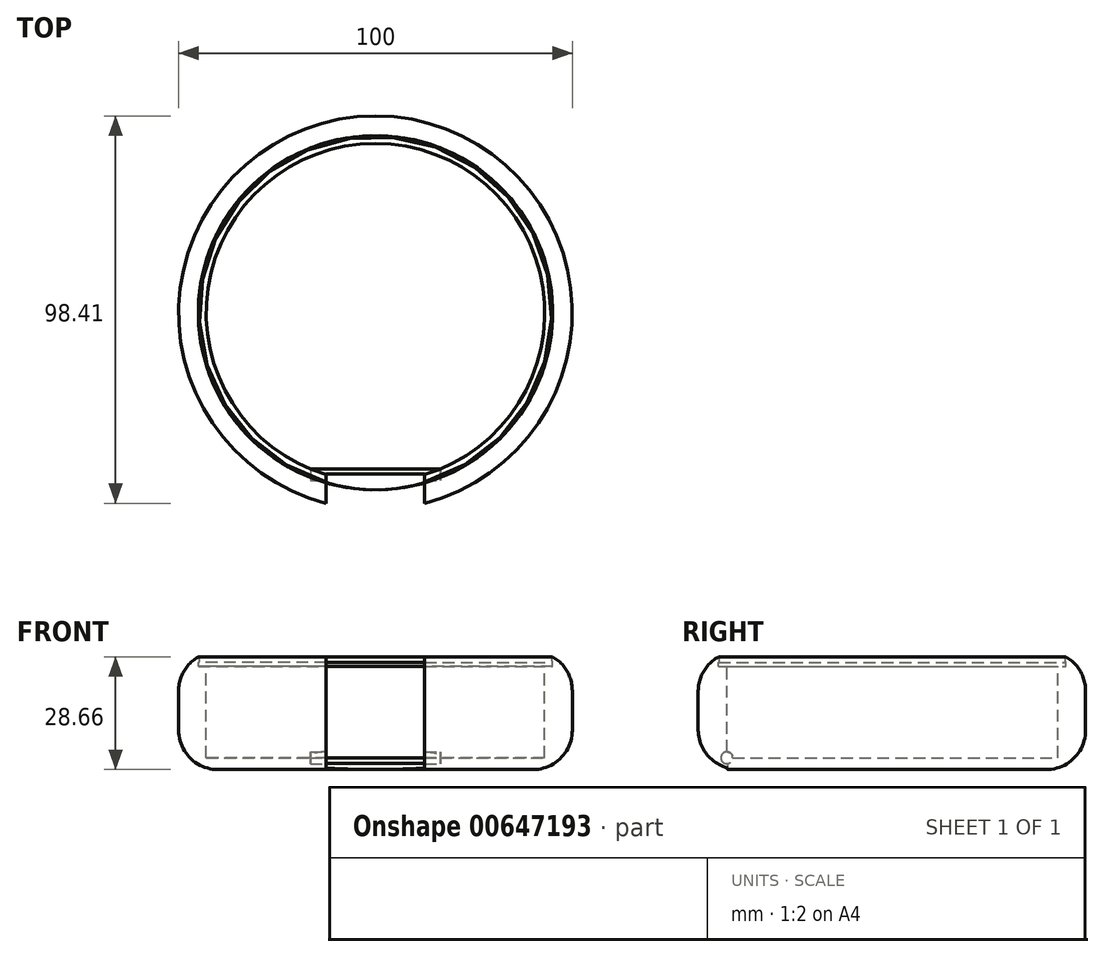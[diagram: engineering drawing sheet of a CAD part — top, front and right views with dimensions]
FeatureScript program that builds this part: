
annotation { "Feature Type Name" : "Feature", "Feature Type Description" : "" }
export const myFeature = defineFeature(function(context is Context, id is Id, definition is map)
    precondition{}
    {
        {
            var Q0;
            Q0=qCreatedBy(makeId("Top.planeOp"),FACE);
            var sketch = newSketch(context, id + "F0", { "sketchPlane" : qUnion([Q0])});
            skCircle(sketch, "E0", {"center": v(0, 0) * mm, "radius": 50 * mm});
            skSolve(sketch);
        }
        {
            var Q0;
            Q0=makeQuery(id+"F0.imprint","IMPRINT",FACE,{"disambiguationData":[TD([[makeQuery(id+"F0.imprint","IMPRINT",EDGE,{"derivedFrom":sQuery(id+"F0.wireOp",EDGE,"E0")}),1.0]])]});
            extrude(context, id + "F1", {"entities" : qUnion([Q0]), "depth" : 30 * mm, "offsetDistance" : 25 * mm});
        }
        {
            var Q0;
            Q0=makeQuery(id+"F1.opExtrude","CAP_FACE",FACE,{"disambiguationData":[OSD([sQuery(id+"F0.wireOp",EDGE,"E0")])],"isStart":false});
            var Q1;
            Q1=makeQuery(id+"F1.opExtrude","CAP_EDGE",EDGE,{"disambiguationData":[OSD([sQuery(id+"F0.wireOp",EDGE,"E0")])],"isStart":true});
            fillet(context, id + "F2", {"entities" : qUnion([Q0, Q1]), "radius" : 10 * mm, "tangentPropagation" : true, "allowEdgeOverflow" : false});
        }
        {
            var Q0;
            Q0=makeQuery(id+"F1.opExtrude","CAP_FACE",FACE,{"disambiguationData":[OSD([sQuery(id+"F0.wireOp",EDGE,"E0")])],"isStart":false});
            var sketch = newSketch(context, id + "F3", { "sketchPlane" : qUnion([Q0])});
            skCircle(sketch, "E1", {"center": v(0, 0) * mm, "radius": 43 * mm});
            skSolve(sketch);
        }
        {
            var Q0;
            Q0 = qSketchRegion(id + "F3", true);
            extrude(context, id + "F4", {"entities" : qUnion([Q0]), "operationType" : NewBodyOperationType.REMOVE, "oppositeDirection" : true, "depth" : 27 * mm, "offsetDistance" : 25 * mm});
        }
        {
            var Q0;
            Q0=qCreatedBy(makeId("Front.planeOp"),FACE);
            cPlane(context, id + "F5", {"entities" : qUnion([Q0]), "cplaneType" : CPlaneType.OFFSET, "offset" : 50 * mm, "width" : 150 * mm, "height" : 150 * mm});
        }
        {
            var Q0;
            Q0=qCreatedBy(id+"F5.planeOp",FACE);
            var sketch = newSketch(context, id + "F6", { "sketchPlane" : qUnion([Q0])});
            skLineSegment(sketch, "E2", {"start": v(0, 0) * mm, "end": v(0, 30) * mm});
            skLineSegment(sketch, "E3", {"start": v(0, 30) * mm, "end": v(12.5, 30) * mm});
            skLineSegment(sketch, "E4", {"start": v(12.5, 30) * mm, "end": v(12.5, 0) * mm});
            skLineSegment(sketch, "E5", {"start": v(12.5, 0) * mm, "end": v(0, 0) * mm});
            skLineSegment(sketch, "E6", {"start": v(0, 30) * mm, "end": v(-12.5, 30) * mm});
            skLineSegment(sketch, "E7", {"start": v(-12.5, 30) * mm, "end": v(-12.5, 0) * mm});
            skLineSegment(sketch, "E8", {"start": v(-12.5, 0) * mm, "end": v(0, 0) * mm});
            skSolve(sketch);
        }
        {
            var Q0;
            Q0 = qSketchRegion(id + "F6", true);
            extrude(context, id + "F7", {"entities" : qUnion([Q0]), "operationType" : NewBodyOperationType.REMOVE, "oppositeDirection" : true, "depth" : 9 * mm, "offsetDistance" : 25 * mm});
        }
        {
            var Q0;
            Q0=qCreatedBy(makeId("Top.planeOp"),FACE);
            cPlane(context, id + "F8", {"entities" : qUnion([Q0]), "cplaneType" : CPlaneType.OFFSET, "offset" : 30 * mm, "width" : 150 * mm, "height" : 150 * mm});
        }
        {
            var Q0;
            Q0=qCreatedBy(id+"F8.planeOp",FACE);
            var sketch = newSketch(context, id + "F9", { "sketchPlane" : qUnion([Q0])});
            skCircle(sketch, "E9", {"center": v(0, 0) * mm, "radius": 45 * mm});
            skSolve(sketch);
        }
        {
            var Q0;
            Q0=makeQuery(id+"F9.imprint","IMPRINT",FACE,{"disambiguationData":[TD([[makeQuery(id+"F9.imprint","IMPRINT",EDGE,{"derivedFrom":sQuery(id+"F9.wireOp",EDGE,"E9")}),1.0]])]});
            extrude(context, id + "F10", {"entities" : qUnion([Q0]), "operationType" : NewBodyOperationType.REMOVE, "oppositeDirection" : true, "depth" : 3.85 * mm, "offsetDistance" : 25 * mm});
        }
        {
            var Q0;
            Q0=makeQuery(id+"F7.boolean.opBoolean","COPY",FACE,{"derivedFrom":makeQuery(id+"F7.opExtrude","SWEPT_FACE",FACE,{"disambiguationData":[OSD([sQuery(id+"F6.wireOp",EDGE,"E7")])]})});
            cPlane(context, id + "F11", {"entities" : qUnion([Q0]), "cplaneType" : CPlaneType.OFFSET, "offset" : 0 * mm, "width" : 150 * mm, "height" : 150 * mm});
        }
        {
            var Q0;
            Q0=qCreatedBy(id+"F11.planeOp",FACE);
            var sketch = newSketch(context, id + "F12", { "sketchPlane" : qUnion([Q0])});
            skCircle(sketch, "E10", {"center": v(-41.14, 3) * mm, "radius": 1.5 * mm});
            skSolve(sketch);
        }
        {
            var Q0;
            Q0=makeQuery(id+"F12.imprint","IMPRINT",FACE,{"disambiguationData":[TD([[makeQuery(id+"F12.imprint","IMPRINT",EDGE,{"derivedFrom":sQuery(id+"F12.wireOp",EDGE,"E10")}),1.0]])]});
            extrude(context, id + "F13", {"entities" : qUnion([Q0]), "operationType" : NewBodyOperationType.REMOVE, "oppositeDirection" : true, "depth" : 4 * mm, "offsetDistance" : 25 * mm});
        }
        {
            var Q0;
            Q0=makeQuery(id+"F12.imprint","IMPRINT",FACE,{"disambiguationData":[TD([[makeQuery(id+"F12.imprint","IMPRINT",EDGE,{"derivedFrom":sQuery(id+"F12.wireOp",EDGE,"E10")}),1.0]])]});
            extrude(context, id + "F14", {"entities" : qUnion([Q0]), "operationType" : NewBodyOperationType.REMOVE, "depth" : 29 * mm, "offsetDistance" : 25 * mm});
        }
        {
            var Q0;
            Q0=qCreatedBy(id+"F11.planeOp",FACE);
            var sketch = newSketch(context, id + "F15", { "sketchPlane" : qUnion([Q0])});
            skArc(sketch, "E11", {"start": v(-43.23, 27.16) * mm, "mid": v(-42.98, 27.91) * mm, "end": v(-43.23, 28.66) * mm});
            skLineSegment(sketch, "E12", {"start": v(-43.23, 28.66) * mm, "end": v(-43.23, 27.16) * mm});
            skSolve(sketch);
        }
        {
            var Q0;
            Q0=qCreatedBy(makeId("Right.planeOp"),FACE);
            var sketch = newSketch(context, id + "F16", { "sketchPlane" : qUnion([Q0])});
            skLineSegment(sketch, "E13", {"start": v(0, 0) * mm, "end": v(0, 49.15) * mm});
            skSolve(sketch);
        }
        {
            var Q0;
            Q0 = qSketchRegion(id + "F15", true);
            var Q1;
            Q1=sQuery(id+"F16.wireOp",EDGE,"E13");
            revolve(context, id + "F17", {"operationType" : NewBodyOperationType.ADD, "surfaceOperationType" : NewSurfaceOperationType.NEW, "entities" : qUnion([Q0]), "axis" : qUnion([Q1]), "revolveType" : RevolveType.FULL});
        }
        {
            var Q0;
            Q0 = qSketchRegion(id + "F6", true);
            extrude(context, id + "F18", {"entities" : qUnion([Q0]), "operationType" : NewBodyOperationType.REMOVE, "oppositeDirection" : true, "depth" : 9 * mm, "offsetDistance" : 25 * mm});
        }
    });
